# Revit family: xCorner_Waste_Receptacle-Bobrick-Surface_Mounted-B-268
name_source: partatom
category: Specialty Equipment
revit_build: Autodesk Revit 2014 (Build: 20130308_1515(x64)
units: mm (PartAtom-declared; Revit-internal decimal feet)

## types (1)
- B-268
    Assembly Code = E2010
    Default Elevation = 40"
    Description = Surface-Mounted Corner Waste Receptacle
    Height = 23"
    Installation Type = Surface Mounted
    Length = 20 9/16"
    Manufacturer = Bobrick
    Material = Metal-Bobrick-304-Stainless Steel-Satin finish

Metal-Bobrick-304-Stainless Steel-Satin finish
    Model = B-268
    Price = Prices may vary. Please consult Manufacturer Representative for most up-to-date price list.
    Product Page URL = http://www.bobrick.com
    Specification = Surface-mounted corner waste receptacle shall be constructed of type 304, 22 gauge (0.8mm) stainless steel with all-welded construction; exposed surfaces shall have satin finish. Top and bottom edges shall be hemmed for safety. Waste receptacle shall have three spot-welded interior hooks and two hooks adhered to the front for attaching the vinyl liner. Waste receptacle shall have a capacity of 1.8 cu. ft. (13.4 gallons) and be furnished with a vinyl liner.
    URL = http://www.bobrick.com
    Width = 14 9/16"

## geometry (parser evidence)
native form markers: Sweep x1
no freeform markers — native parametric forms only
